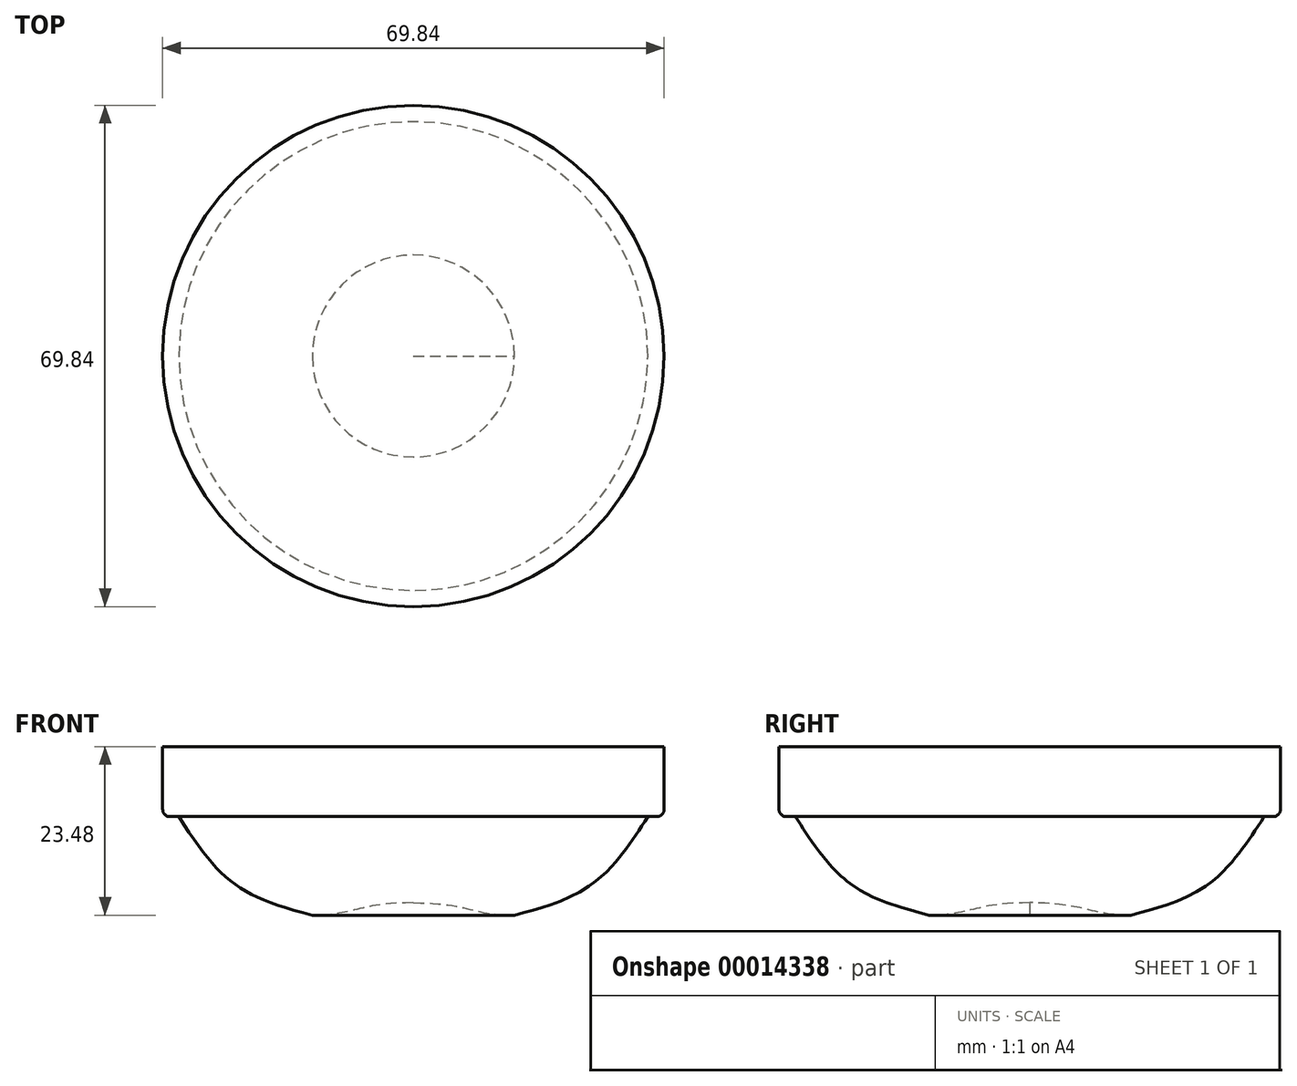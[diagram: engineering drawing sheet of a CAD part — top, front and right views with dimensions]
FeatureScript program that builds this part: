
annotation { "Feature Type Name" : "Feature", "Feature Type Description" : "" }
export const myFeature = defineFeature(function(context is Context, id is Id, definition is map)
    precondition{}
    {
        {
            var Q0;
            Q0=qCreatedBy(makeId("Front.planeOp"),FACE);
            var sketch = newSketch(context, id + "F0", { "sketchPlane" : qUnion([Q0])});
            skLineSegment(sketch, "E0", {"start": v(0, 0) * mm, "end": v(0, 23.48) * mm});
            skLineSegment(sketch, "E1", {"start": v(0, 23.48) * mm, "end": v(34.92, 23.48) * mm});
            skLineSegment(sketch, "E2", {"start": v(34.92, 23.48) * mm, "end": v(34.92, 13.73) * mm});
            skLineSegment(sketch, "E3", {"start": v(34.92, 13.73) * mm, "end": v(32.66, 13.73) * mm});
            skFitSpline(sketch, "E4", {"points": [v(32.66, 13.73) * mm, v(14.06, 0) * mm], "startDerivative": vector(-17.1, -26.64) * mm, "endDerivative": vector(-31.51, -7.96) * mm});
            skFitSpline(sketch, "E5", {"points": [v(0, 1.73) * mm, v(14.06, 0) * mm], "startDerivative": vector(23.36, 0) * mm, "endDerivative": vector(18.26, 0) * mm});
            skSolve(sketch);
        }
        {
            var Q0;
            {var subQ1=sQuery(id+"F0.wireOp",EDGE,"E1");Q0=makeQuery(id+"F0.imprint","IMPRINT",FACE,{"disambiguationData":[TD([[makeQuery(id+"F0.imprint","IMPRINT",EDGE,{"derivedFrom":subQ1}),-1.0]])]});}
            var Q1;
            Q1=sQuery(id+"F0.wireOp",EDGE,"E0");
            revolve(context, id + "F1", {"entities" : qUnion([Q0]), "axis" : qUnion([Q1]), "revolveType" : RevolveType.FULL});
        }
        {
            var Q0;
            Q0=makeQuery(id+"F1.opRevolve","SWEPT_EDGE",EDGE,{"disambiguationData":[OSD([sQuery(id+"F0.wireOp",EDGE,"E2"),sQuery(id+"F0.wireOp",EDGE,"E3")])]});
            fillet(context, id + "F2", {"entities" : qUnion([Q0]), "radius" : 1 * mm, "tangentPropagation" : true, "allowEdgeOverflow" : false});
        }
    });
